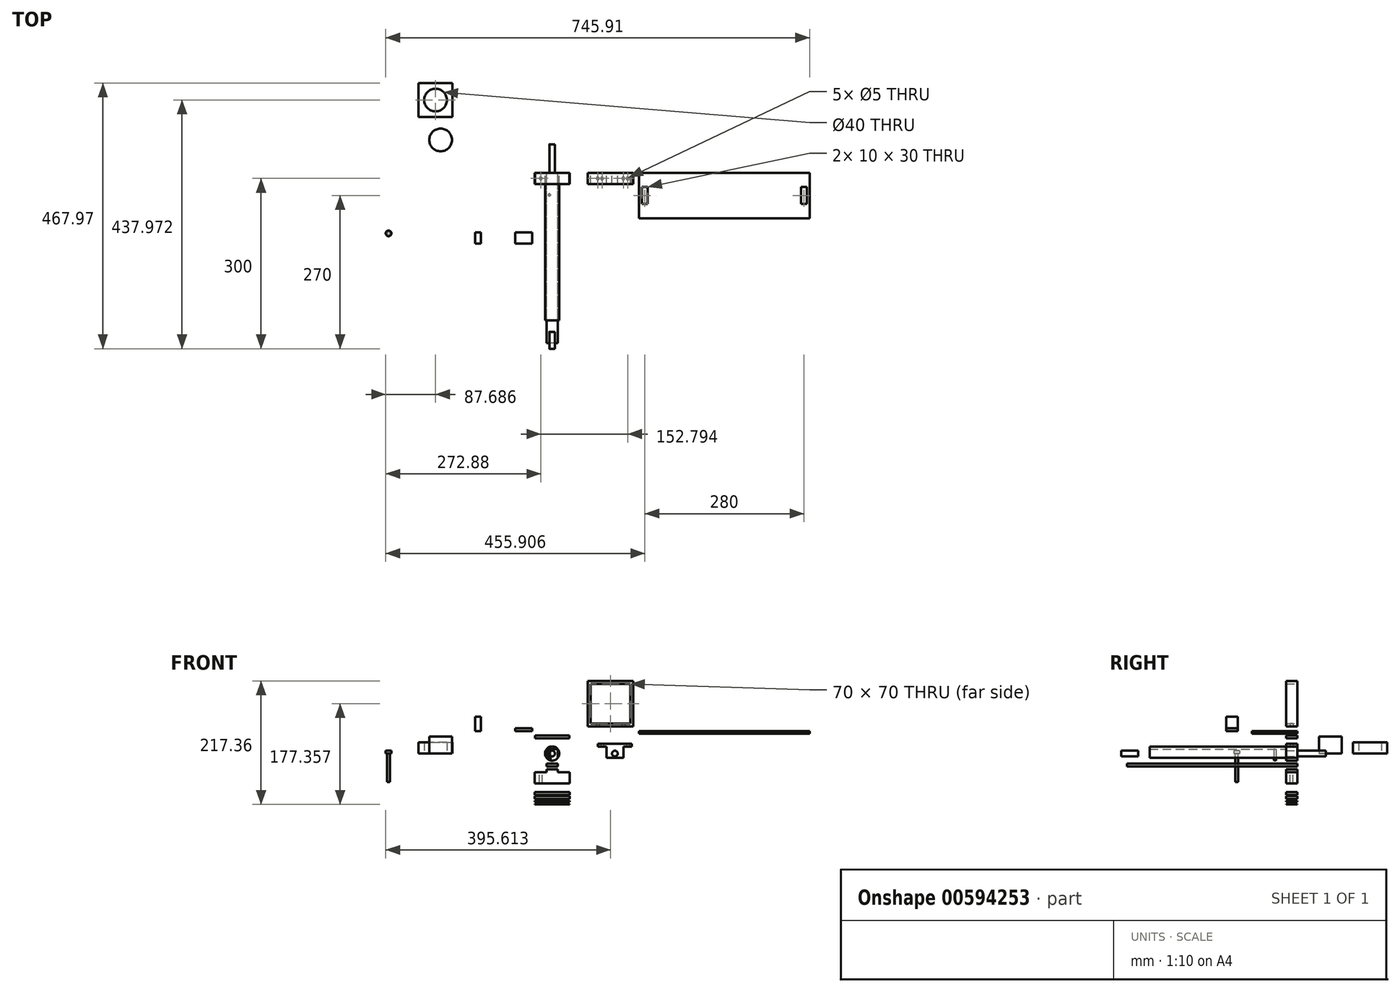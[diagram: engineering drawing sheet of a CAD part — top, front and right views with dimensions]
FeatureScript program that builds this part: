
annotation { "Feature Type Name" : "Feature", "Feature Type Description" : "" }
export const myFeature = defineFeature(function(context is Context, id is Id, definition is map)
    precondition{}
    {
        {
            var Q0;
            Q0=qCreatedBy(makeId("Front.planeOp"),FACE);
            var sketch = newSketch(context, id + "F0", { "sketchPlane" : qUnion([Q0])});
            skCircle(sketch, "E0", {"center": v(0, 0) * mm, "radius": 12.5 * mm});
            skCircle(sketch, "E1", {"center": v(110.3, 0) * mm, "radius": 5 * mm});
            skLineSegment(sketch, "E2.bottom", {"start": v(-30, 31.74) * mm, "end": v(30, 31.74) * mm});
            skLineSegment(sketch, "E2.top", {"start": v(-30, 26.74) * mm, "end": v(30, 26.74) * mm});
            skLineSegment(sketch, "E2.left", {"start": v(-30, 31.74) * mm, "end": v(-30, 26.74) * mm});
            skLineSegment(sketch, "E2.right", {"start": v(30, 31.74) * mm, "end": v(30, 26.74) * mm});
            skPoint(sketch, "E2.middle", {"position": v(0, 29.24) * mm});
            skLineSegment(sketch, "E3", {"start": v(110.3, 10) * mm, "end": v(110.3, -10) * mm, "construction": true});
            skCircle(sketch, "E4", {"center": v(110.3, 0) * mm, "radius": 12.5 * mm, "construction": true});
            skLineSegment(sketch, "E5", {"start": v(97.8, 0) * mm, "end": v(122.8, 0) * mm, "construction": true});
            skLineSegment(sketch, "E6", {"start": v(110.3, 12.5) * mm, "end": v(79.29, 12.5) * mm, "construction": true});
            skLineSegment(sketch, "E7", {"start": v(110.3, 5) * mm, "end": v(79.29, 5) * mm, "construction": true});
            skLineSegment(sketch, "E8", {"start": v(110.3, -5) * mm, "end": v(79.29, -5) * mm, "construction": true});
            skLineSegment(sketch, "E9", {"start": v(110.3, -12.5) * mm, "end": v(79.29, -12.5) * mm, "construction": true});
            skLineSegment(sketch, "E10", {"start": v(110.3, -7.5) * mm, "end": v(125.3, -7.5) * mm});
            skLineSegment(sketch, "E11", {"start": v(110.3, 17.5) * mm, "end": v(140.3, 17.5) * mm});
            skLineSegment(sketch, "E12", {"start": v(125.3, 12.5) * mm, "end": v(140.3, 12.5) * mm});
            skLineSegment(sketch, "E13", {"start": v(125.3, -7.5) * mm, "end": v(125.3, 12.5) * mm});
            skLineSegment(sketch, "E14", {"start": v(140.3, 17.5) * mm, "end": v(140.3, 12.5) * mm});
            skPoint(sketch, "E15.orphan", {"position": v(110.3, 12.5) * mm});
            skLineSegment(sketch, "E16.MirrorCS", {"start": v(95.3, 12.5) * mm, "end": v(80.3, 12.5) * mm});
            skLineSegment(sketch, "E17.MirrorCS", {"start": v(80.3, 17.5) * mm, "end": v(80.3, 12.5) * mm});
            skLineSegment(sketch, "E18.MirrorCS", {"start": v(110.3, 17.5) * mm, "end": v(80.3, 17.5) * mm});
            skLineSegment(sketch, "E19.MirrorCS", {"start": v(95.3, -7.5) * mm, "end": v(95.3, 12.5) * mm});
            skLineSegment(sketch, "E20.MirrorCS", {"start": v(110.3, -7.5) * mm, "end": v(95.3, -7.5) * mm});
            skLineSegment(sketch, "E21.top", {"start": v(0, -27.58) * mm, "end": v(10, -27.58) * mm});
            skLineSegment(sketch, "E22", {"start": v(10.93, -32.58) * mm, "end": v(30.93, -32.58) * mm});
            skLineSegment(sketch, "E23", {"start": v(30.93, -32.58) * mm, "end": v(30.93, -52.58) * mm});
            skLineSegment(sketch, "E24", {"start": v(30.93, -52.58) * mm, "end": v(0, -52.58) * mm});
            skLineSegment(sketch, "E25.MirrorCS", {"start": v(0, -27.58) * mm, "end": v(-10, -27.58) * mm});
            skLineSegment(sketch, "E26.MirrorCS", {"start": v(-10.93, -32.58) * mm, "end": v(-30.93, -32.58) * mm});
            skLineSegment(sketch, "E27.MirrorCS", {"start": v(-30.93, -32.58) * mm, "end": v(-30.93, -52.58) * mm});
            skLineSegment(sketch, "E28.MirrorCS", {"start": v(-30.93, -52.58) * mm, "end": v(0, -52.58) * mm});
            skLineSegment(sketch, "E29", {"start": v(0, -22.52) * mm, "end": v(10, -22.52) * mm});
            skLineSegment(sketch, "E30", {"start": v(10, -22.52) * mm, "end": v(10, -17.52) * mm});
            skLineSegment(sketch, "E31", {"start": v(10, -17.52) * mm, "end": v(0, -17.52) * mm});
            skLineSegment(sketch, "E32.MirrorCS", {"start": v(-10, -17.52) * mm, "end": v(0, -17.52) * mm});
            skLineSegment(sketch, "E33.MirrorCS", {"start": v(0, -22.52) * mm, "end": v(-10, -22.52) * mm});
            skLineSegment(sketch, "E34.MirrorCS", {"start": v(-10, -22.52) * mm, "end": v(-10, -17.52) * mm});
            skLineSegment(sketch, "E35.bottom", {"start": v(137.73, 52.7) * mm, "end": v(67.73, 52.7) * mm});
            skLineSegment(sketch, "E35.top", {"start": v(137.73, 122.7) * mm, "end": v(67.73, 122.7) * mm});
            skLineSegment(sketch, "E35.left", {"start": v(137.73, 52.7) * mm, "end": v(137.73, 122.7) * mm});
            skLineSegment(sketch, "E35.right", {"start": v(67.73, 52.7) * mm, "end": v(67.73, 122.7) * mm});
            skPoint(sketch, "E35.middle", {"position": v(102.73, 87.7) * mm});
            skLineSegment(sketch, "E36.bottom", {"start": v(62.73, 127.7) * mm, "end": v(142.73, 127.7) * mm});
            skLineSegment(sketch, "E36.top", {"start": v(62.73, 47.7) * mm, "end": v(142.73, 47.7) * mm});
            skLineSegment(sketch, "E36.left", {"start": v(62.73, 127.7) * mm, "end": v(62.73, 47.7) * mm});
            skLineSegment(sketch, "E36.right", {"start": v(142.73, 127.7) * mm, "end": v(142.73, 47.7) * mm});
            skLineSegment(sketch, "E37.bottom", {"start": v(-30.93, -79.86) * mm, "end": v(30.93, -79.86) * mm});
            skLineSegment(sketch, "E37.top", {"start": v(-30.93, -74.86) * mm, "end": v(30.93, -74.86) * mm});
            skLineSegment(sketch, "E37.left", {"start": v(-30.93, -79.86) * mm, "end": v(-30.93, -74.86) * mm});
            skLineSegment(sketch, "E37.right", {"start": v(30.93, -79.86) * mm, "end": v(30.93, -74.86) * mm});
            skLineSegment(sketch, "E38.MirrorCS", {"start": v(-30.74, -88.65) * mm, "end": v(31.12, -88.65) * mm});
            skLineSegment(sketch, "E39.MirrorCS", {"start": v(-30.74, -89.65) * mm, "end": v(31.12, -89.65) * mm});
            skLineSegment(sketch, "E40", {"start": v(-30.93, -82.76) * mm, "end": v(30.93, -82.76) * mm});
            skLineSegment(sketch, "E41", {"start": v(30.93, -82.76) * mm, "end": v(30.93, -84.76) * mm});
            skLineSegment(sketch, "E42", {"start": v(30.93, -84.76) * mm, "end": v(-30.93, -84.76) * mm});
            skLineSegment(sketch, "E43", {"start": v(-30.93, -84.76) * mm, "end": v(-30.93, -82.76) * mm});
            skLineSegment(sketch, "E44", {"start": v(-30.74, -88.65) * mm, "end": v(-30.74, -89.65) * mm});
            skLineSegment(sketch, "E45", {"start": v(31.12, -88.65) * mm, "end": v(31.12, -89.65) * mm});
            skLineSegment(sketch, "E46", {"start": v(-30.93, -72.74) * mm, "end": v(30.93, -72.74) * mm});
            skLineSegment(sketch, "E47", {"start": v(30.93, -72.74) * mm, "end": v(30.93, -67.74) * mm});
            skLineSegment(sketch, "E48", {"start": v(30.93, -67.74) * mm, "end": v(-30.93, -67.74) * mm});
            skLineSegment(sketch, "E49", {"start": v(-30.93, -67.74) * mm, "end": v(-30.93, -72.74) * mm});
            skLineSegment(sketch, "E50", {"start": v(-10, -27.58) * mm, "end": v(-10, -32.58) * mm});
            skLineSegment(sketch, "E51", {"start": v(-10, -32.58) * mm, "end": v(-10.93, -32.58) * mm});
            skPoint(sketch, "E52.MirrorCS.end.orphan", {"position": v(-10, -27.58) * mm});
            skPoint(sketch, "E52.MirrorCS.start.orphan", {"position": v(-10.93, -32.58) * mm});
            skLineSegment(sketch, "E53", {"start": v(10, -27.58) * mm, "end": v(10, -32.58) * mm});
            skLineSegment(sketch, "E54", {"start": v(10, -32.58) * mm, "end": v(10.93, -32.58) * mm});
            skLineSegment(sketch, "E55.left", {"start": v(194.47, 95.4) * mm, "end": v(194.47, 97.9) * mm});
            skLineSegment(sketch, "E56.bottom", {"start": v(-122.7, 157) * mm, "end": v(-422.7, 157) * mm});
            skLineSegment(sketch, "E56.top", {"start": v(-122.7, 159.5) * mm, "end": v(-422.7, 159.5) * mm});
            skLineSegment(sketch, "E56.left", {"start": v(-122.7, 157) * mm, "end": v(-122.7, 159.5) * mm});
            skLineSegment(sketch, "E56.right", {"start": v(-422.7, 157) * mm, "end": v(-422.7, 159.5) * mm});
            skLineSegment(sketch, "E57", {"start": v(-272.7, 150) * mm, "end": v(-272.7, 153.49) * mm, "construction": true});
            skPoint(sketch, "E57.startSnap0", {"position": v(-272.7, 157) * mm});
            skSolve(sketch);
        }
        {
            var Q0;
            Q0=makeQuery(id+"F0.imprint","IMPRINT",FACE,{"disambiguationData":[TD([[makeQuery(id+"F0.imprint","IMPRINT",EDGE,{"derivedFrom":sQuery(id+"F0.wireOp",EDGE,"E1")}),-1.0]])]});
            var Q1;
            Q1=makeQuery(id+"F0.imprint","IMPRINT",FACE,{"disambiguationData":[TD([[makeQuery(id+"F0.imprint","IMPRINT",EDGE,{"derivedFrom":sQuery(id+"F0.wireOp",EDGE,"E2.bottom")}),-1.0]])]});
            var Q2;
            Q2=makeQuery(id+"F0.imprint","IMPRINT",FACE,{"disambiguationData":[TD([[makeQuery(id+"F0.imprint","IMPRINT",EDGE,{"derivedFrom":sQuery(id+"F0.wireOp",EDGE,"E21.top")}),-1.0]])]});
            var Q3;
            Q3=makeQuery(id+"F0.imprint","IMPRINT",FACE,{"disambiguationData":[TD([[makeQuery(id+"F0.imprint","IMPRINT",EDGE,{"derivedFrom":sQuery(id+"F0.wireOp",EDGE,"E35.bottom")}),1.0]])]});
            var Q4;
            Q4=makeQuery(id+"F0.imprint","IMPRINT",FACE,{"disambiguationData":[TD([[makeQuery(id+"F0.imprint","IMPRINT",EDGE,{"derivedFrom":sQuery(id+"F0.wireOp",EDGE,"E37.bottom")}),1.0]])]});
            var Q5;
            Q5=makeQuery(id+"F0.imprint","IMPRINT",FACE,{"disambiguationData":[TD([[makeQuery(id+"F0.imprint","IMPRINT",EDGE,{"derivedFrom":sQuery(id+"F0.wireOp",EDGE,"E38.MirrorCS")}),-1.0]])]});
            var Q6;
            Q6=makeQuery(id+"F0.imprint","IMPRINT",FACE,{"disambiguationData":[TD([[makeQuery(id+"F0.imprint","IMPRINT",EDGE,{"derivedFrom":sQuery(id+"F0.wireOp",EDGE,"E40")}),-1.0]])]});
            var Q7;
            Q7=makeQuery(id+"F0.imprint","IMPRINT",FACE,{"disambiguationData":[TD([[makeQuery(id+"F0.imprint","IMPRINT",EDGE,{"derivedFrom":sQuery(id+"F0.wireOp",EDGE,"E46")}),1.0]])]});
            var Q8;
            {var subQ5=sQuery(id+"F0.wireOp",EDGE,"E55.right");Q8=makeQuery(id+"F0.imprint","IMPRINT",FACE,{"disambiguationData":[TD([[makeQuery(id+"F0.imprint","IMPRINT",EDGE,{"derivedFrom":subQ5}),-1.0]])]});}
            extrude(context, id + "F1", {"entities" : qUnion([Q0, Q1, Q2, Q3, Q4, Q5, Q6, Q7, Q8]), "depth" : 20 * mm, "offsetDistance" : 25 * mm});
        }
        {
            var Q0;
            Q0=makeQuery(id+"F0.imprint","IMPRINT",FACE,{"disambiguationData":[TD([[makeQuery(id+"F0.imprint","IMPRINT",EDGE,{"derivedFrom":sQuery(id+"F0.wireOp",EDGE,"E0")}),1.0]])]});
            extrude(context, id + "F2", {"entities" : qUnion([Q0]), "depth" : 260 * mm, "offsetDistance" : 25 * mm});
        }
        {
            var Q0;
            Q0=makeQuery(id+"F2.opExtrude","CAP_FACE",FACE,{"disambiguationData":[OSD([sQuery(id+"F0.wireOp",EDGE,"E0")])],"isStart":false});
            var sketch = newSketch(context, id + "F3", { "sketchPlane" : qUnion([Q0])});
            skCircle(sketch, "E58", {"center": v(0, 0) * mm, "radius": 5 * mm});
            skSolve(sketch);
        }
        {
            var Q0;
            Q0=makeQuery(id+"F3.imprint","IMPRINT",FACE,{"disambiguationData":[TD([[makeQuery(id+"F3.imprint","IMPRINT",EDGE,{"derivedFrom":sQuery(id+"F3.wireOp",EDGE,"E58")}),1.0]])]});
            extrude(context, id + "F4", {"entities" : qUnion([Q0]), "operationType" : NewBodyOperationType.ADD, "depth" : 50 * mm, "offsetDistance" : 25 * mm});
        }
        {
            var Q0;
            Q0=makeQuery(id+"F0.imprint","IMPRINT",FACE,{"disambiguationData":[TD([[makeQuery(id+"F0.imprint","IMPRINT",EDGE,{"derivedFrom":sQuery(id+"F0.wireOp",EDGE,"E29")}),1.0]])]});
            extrude(context, id + "F5", {"entities" : qUnion([Q0]), "depth" : 300 * mm, "offsetDistance" : 25 * mm});
        }
        {
            var Q0;
            Q0=makeQuery(id+"F1.opExtrude","SWEPT_FACE",FACE,{"disambiguationData":[OSD([sQuery(id+"F0.wireOp",EDGE,"E26.MirrorCS")])]});
            var sketch = newSketch(context, id + "F6", { "sketchPlane" : qUnion([Q0])});
            skCircle(sketch, "E59", {"center": v(-20, -10) * mm, "radius": 2.5 * mm});
            skSolve(sketch);
        }
        {
            var Q0;
            Q0=makeQuery(id+"F6.imprint","IMPRINT",FACE,{"disambiguationData":[TD([[makeQuery(id+"F6.imprint","IMPRINT",EDGE,{"derivedFrom":sQuery(id+"F6.wireOp",EDGE,"E59")}),1.0]])]});
            var Q1;
            Q1=makeQuery(id+"FNYWGUJzlf6PVvf_4.imprint","IMPRINT",FACE,{"disambiguationData":[TD([[makeQuery(id+"FNYWGUJzlf6PVvf_4.imprint","IMPRINT",EDGE,{"derivedFrom":sQuery(id+"FNYWGUJzlf6PVvf_4.wireOp",EDGE,"JrdPBHnR-5tIZ-cZ5f-IPz8-CMVoVNEgzM20")}),1.0]])]});
            extrude(context, id + "F7", {"entities" : qUnion([Q0, Q1]), "operationType" : NewBodyOperationType.REMOVE, "oppositeDirection" : true, "depth" : 25 * mm, "offsetDistance" : 25 * mm});
        }
        {
            var Q0;
            Q0=makeQuery(id+"F1.opExtrude","SWEPT_FACE",FACE,{"disambiguationData":[OSD([sQuery(id+"F0.wireOp",EDGE,"E12")])]});
            var sketch = newSketch(context, id + "F8", { "sketchPlane" : qUnion([Q0])});
            skCircle(sketch, "E60", {"center": v(132.8, 10) * mm, "radius": 2.5 * mm});
            skPoint(sketch, "E60.centerSnap0", {"position": v(132.8, 20) * mm});
            skPoint(sketch, "E60.centerSnap1", {"position": v(125.3, 10) * mm});
            skSolve(sketch);
        }
        {
            var Q0;
            Q0=makeQuery(id+"F1.opExtrude","SWEPT_FACE",FACE,{"disambiguationData":[OSD([sQuery(id+"F0.wireOp",EDGE,"E16.MirrorCS")])]});
            var sketch = newSketch(context, id + "F9", { "sketchPlane" : qUnion([Q0])});
            skCircle(sketch, "E61", {"center": v(87.8, 10) * mm, "radius": 2.5 * mm});
            skPoint(sketch, "E61.centerSnap0", {"position": v(80.3, 10) * mm});
            skPoint(sketch, "E61.centerSnap1", {"position": v(87.8, 20) * mm});
            skSolve(sketch);
        }
        {
            var Q0;
            Q0=makeQuery(id+"F9.imprint","IMPRINT",FACE,{"disambiguationData":[TD([[makeQuery(id+"F9.imprint","IMPRINT",EDGE,{"derivedFrom":sQuery(id+"F9.wireOp",EDGE,"E61")}),1.0]])]});
            var Q1;
            Q1=makeQuery(id+"F8.imprint","IMPRINT",FACE,{"disambiguationData":[TD([[makeQuery(id+"F8.imprint","IMPRINT",EDGE,{"derivedFrom":sQuery(id+"F8.wireOp",EDGE,"E60")}),1.0]])]});
            extrude(context, id + "F10", {"entities" : qUnion([Q0, Q1]), "operationType" : NewBodyOperationType.REMOVE, "oppositeDirection" : true, "depth" : 25 * mm, "offsetDistance" : 25 * mm});
        }
        {
            var Q0;
            Q0=makeQuery(id+"F5.opExtrude","SWEPT_FACE",FACE,{"disambiguationData":[OSD([sQuery(id+"F0.wireOp",EDGE,"E31"),sQuery(id+"F0.wireOp",EDGE,"E32.MirrorCS")])]});
            var sketch = newSketch(context, id + "F11", { "sketchPlane" : qUnion([Q0])});
            skLineSegment(sketch, "E62", {"start": v(-10, -280) * mm, "end": v(10, -280) * mm});
            skCircle(sketch, "E63", {"center": v(5, -39.13) * mm, "radius": 1.93 * mm});
            skPoint(sketch, "E64.orphan", {"position": v(0, -300) * mm});
            skCircle(sketch, "E65.MirrorC", {"center": v(-5, -39.13) * mm, "radius": 1.93 * mm});
            skLineSegment(sketch, "E66", {"start": v(10, -20) * mm, "end": v(-10, -20) * mm});
            skSolve(sketch);
        }
        {
            var Q0;
            Q0=makeQuery(id+"F11.imprint","IMPRINT",FACE,{"disambiguationData":[TD([[makeQuery(id+"F11.imprint","IMPRINT",EDGE,{"derivedFrom":sQuery(id+"F11.wireOp",EDGE,"E65.MirrorC")}),-1.0]])]});
            var Q1;
            Q1=makeQuery(id+"F11.imprint","IMPRINT",FACE,{"disambiguationData":[TD([[makeQuery(id+"F11.imprint","IMPRINT",EDGE,{"derivedFrom":sQuery(id+"F11.wireOp",EDGE,"E63")}),1.0]])]});
            extrude(context, id + "F12", {"entities" : qUnion([Q0, Q1]), "operationType" : NewBodyOperationType.REMOVE, "depth" : 25 * mm, "offsetDistance" : 25 * mm});
        }
        {
            var Q0;
            Q0=makeQuery(id+"F1.opExtrude","SWEPT_FACE",FACE,{"disambiguationData":[OSD([sQuery(id+"F0.wireOp",EDGE,"E36.top")])]});
            var sketch = newSketch(context, id + "F13", { "sketchPlane" : qUnion([Q0])});
            skCircle(sketch, "E67", {"center": v(80.23, 10) * mm, "radius": 2.5 * mm});
            skCircle(sketch, "E68", {"center": v(125.23, 10) * mm, "radius": 2.5 * mm});
            skLineSegment(sketch, "E69", {"start": v(62.73, 20) * mm, "end": v(142.73, 20) * mm, "construction": true});
            skLineSegment(sketch, "E70", {"start": v(142.73, 20) * mm, "end": v(142.73, 0) * mm, "construction": true});
            skLineSegment(sketch, "E71", {"start": v(142.73, 0) * mm, "end": v(62.73, 0) * mm, "construction": true});
            skLineSegment(sketch, "E72", {"start": v(62.73, 0) * mm, "end": v(62.73, 20) * mm, "construction": true});
            skLineSegment(sketch, "E73", {"start": v(67.73, 20) * mm, "end": v(67.73, 0) * mm, "construction": true});
            skLineSegment(sketch, "E74", {"start": v(137.73, 20) * mm, "end": v(137.73, 0) * mm, "construction": true});
            skSolve(sketch);
        }
        {
            var Q0;
            Q0=makeQuery(id+"F2.opExtrude","CAP_FACE",FACE,{"disambiguationData":[OSD([sQuery(id+"F0.wireOp",EDGE,"E0")])],"isStart":true});
            var sketch = newSketch(context, id + "F14", { "sketchPlane" : qUnion([Q0])});
            skCircle(sketch, "E75", {"center": v(0, 0) * mm, "radius": 5 * mm});
            skSolve(sketch);
        }
        {
            var Q0;
            Q0=qSketchRegion(id+"F14",true);
            extrude(context, id + "F15", {"entities" : qUnion([Q0]), "operationType" : NewBodyOperationType.ADD, "depth" : 50 * mm, "offsetDistance" : 25 * mm});
        }
        {
            var Q0;
            Q0=qCreatedBy(makeId("Front.planeOp"),FACE);
            var sketch = newSketch(context, id + "F16", { "sketchPlane" : qUnion([Q0])});
            skLineSegment(sketch, "E76.bottom", {"start": v(153.03, 39.78) * mm, "end": v(453.03, 39.78) * mm});
            skLineSegment(sketch, "E76.top", {"start": v(153.03, 34.78) * mm, "end": v(453.03, 34.78) * mm});
            skLineSegment(sketch, "E76.left", {"start": v(153.03, 39.78) * mm, "end": v(153.03, 34.78) * mm});
            skLineSegment(sketch, "E76.right", {"start": v(453.03, 39.78) * mm, "end": v(453.03, 34.78) * mm});
            skSolve(sketch);
        }
        {
            var Q0;
            Q0=makeQuery(id+"F16.imprint","IMPRINT",FACE,{"disambiguationData":[TD([[makeQuery(id+"F16.imprint","IMPRINT",EDGE,{"derivedFrom":sQuery(id+"F16.wireOp",EDGE,"E76.bottom")}),-1.0]])]});
            extrude(context, id + "F17", {"entities" : qUnion([Q0]), "depth" : 80 * mm, "offsetDistance" : 25 * mm});
        }
        {
            var Q0;
            Q0=makeQuery(id+"F17.opExtrude","SWEPT_FACE",FACE,{"disambiguationData":[OSD([sQuery(id+"F16.wireOp",EDGE,"E76.bottom")])]});
            var sketch = newSketch(context, id + "F18", { "sketchPlane" : qUnion([Q0])});
            skLineSegment(sketch, "E77", {"start": v(173.03, 0) * mm, "end": v(173.03, -80) * mm});
            skLineSegment(sketch, "E78.bottom", {"start": v(158.03, -25) * mm, "end": v(168.03, -25) * mm});
            skLineSegment(sketch, "E78.top", {"start": v(158.03, -55) * mm, "end": v(168.03, -55) * mm});
            skLineSegment(sketch, "E78.left", {"start": v(158.03, -25) * mm, "end": v(158.03, -55) * mm});
            skLineSegment(sketch, "E78.right", {"start": v(168.03, -25) * mm, "end": v(168.03, -55) * mm});
            skPoint(sketch, "E78.middle", {"position": v(163.03, -40) * mm});
            skLineSegment(sketch, "E79", {"start": v(303.03, 0) * mm, "end": v(303.03, -80) * mm, "construction": true});
            skLineSegment(sketch, "E80.MirrorCS", {"start": v(438.03, -25) * mm, "end": v(438.03, -55) * mm});
            skLineSegment(sketch, "E81.MirrorCS", {"start": v(448.03, -25) * mm, "end": v(438.03, -25) * mm});
            skLineSegment(sketch, "E82.MirrorCS", {"start": v(448.03, -25) * mm, "end": v(448.03, -55) * mm});
            skLineSegment(sketch, "E83.MirrorCS", {"start": v(448.03, -55) * mm, "end": v(438.03, -55) * mm});
            skLineSegment(sketch, "E84.MirrorCS", {"start": v(433.03, 0) * mm, "end": v(433.03, -80) * mm});
            skLineSegment(sketch, "E85.bottom", {"start": v(-65.07, -104.85) * mm, "end": v(-35.07, -104.85) * mm});
            skLineSegment(sketch, "E85.top", {"start": v(-65.07, -124.85) * mm, "end": v(-35.07, -124.85) * mm});
            skLineSegment(sketch, "E85.left", {"start": v(-65.07, -104.85) * mm, "end": v(-65.07, -124.85) * mm});
            skLineSegment(sketch, "E85.right", {"start": v(-35.07, -104.85) * mm, "end": v(-35.07, -124.85) * mm});
            skLineSegment(sketch, "E86.bottom", {"start": v(-135.53, -104.85) * mm, "end": v(-125.53, -104.85) * mm});
            skLineSegment(sketch, "E86.top", {"start": v(-135.53, -124.85) * mm, "end": v(-125.53, -124.85) * mm});
            skLineSegment(sketch, "E86.left", {"start": v(-135.53, -104.85) * mm, "end": v(-135.53, -124.85) * mm});
            skLineSegment(sketch, "E86.right", {"start": v(-125.53, -104.85) * mm, "end": v(-125.53, -124.85) * mm});
            skSolve(sketch);
        }
        {
            var Q0;
            Q0=qCreatedBy(makeId("Top.planeOp"),FACE);
            var sketch = newSketch(context, id + "F19", { "sketchPlane" : qUnion([Q0])});
            skCircle(sketch, "E87", {"center": v(-196.25, 57.8) * mm, "radius": 20 * mm});
            skLineSegment(sketch, "E88.bottom", {"start": v(-235.2, 97.97) * mm, "end": v(-175.2, 97.97) * mm});
            skLineSegment(sketch, "E88.top", {"start": v(-235.2, 157.97) * mm, "end": v(-175.2, 157.97) * mm});
            skLineSegment(sketch, "E88.left", {"start": v(-235.2, 97.97) * mm, "end": v(-235.2, 157.97) * mm});
            skLineSegment(sketch, "E88.right", {"start": v(-175.2, 97.97) * mm, "end": v(-175.2, 157.97) * mm});
            skCircle(sketch, "E89", {"center": v(-205.2, 127.97) * mm, "radius": 20 * mm});
            skPoint(sketch, "E89.centerSnap0", {"position": v(-175.2, 127.97) * mm});
            skPoint(sketch, "E89.centerSnap1", {"position": v(-205.2, 97.97) * mm});
            skSolve(sketch);
        }
        {
            var Q0;
            Q0=makeQuery(id+"F19.imprint","IMPRINT",FACE,{"disambiguationData":[TD([[makeQuery(id+"F19.imprint","IMPRINT",EDGE,{"derivedFrom":sQuery(id+"F19.wireOp",EDGE,"E87")}),1.0]])]});
            extrude(context, id + "F20", {"entities" : qUnion([Q0]), "depth" : 30 * mm, "offsetDistance" : 25 * mm});
        }
        {
            var Q0;
            Q0=makeQuery(id+"F19.imprint","IMPRINT",FACE,{"disambiguationData":[TD([[makeQuery(id+"F19.imprint","IMPRINT",EDGE,{"derivedFrom":sQuery(id+"F19.wireOp",EDGE,"E88.bottom")}),1.0]])]});
            extrude(context, id + "F21", {"entities" : qUnion([Q0]), "depth" : 20 * mm, "offsetDistance" : 25 * mm});
        }
        {
            var Q0;
            Q0=makeQuery(id+"F18.imprint","IMPRINT",FACE,{"disambiguationData":[TD([[makeQuery(id+"F18.imprint","IMPRINT",EDGE,{"derivedFrom":sQuery(id+"F18.wireOp",EDGE,"E78.bottom")}),-1.0]])]});
            var Q1;
            Q1=makeQuery(id+"F18.imprint","IMPRINT",FACE,{"disambiguationData":[TD([[makeQuery(id+"F18.imprint","IMPRINT",EDGE,{"derivedFrom":sQuery(id+"F18.wireOp",EDGE,"E80.MirrorCS")}),1.0]])]});
            extrude(context, id + "F22", {"entities" : qUnion([Q0, Q1]), "operationType" : NewBodyOperationType.REMOVE, "endBound" : BoundingType.THROUGH_ALL, "oppositeDirection" : true, "depth" : 25 * mm, "offsetDistance" : 25 * mm});
        }
        {
            var Q0;
            Q0=makeQuery(id+"F18.imprint","IMPRINT",FACE,{"disambiguationData":[TD([[makeQuery(id+"F18.imprint","IMPRINT",EDGE,{"derivedFrom":sQuery(id+"F18.wireOp",EDGE,"E86.bottom")}),-1.0]])]});
            extrude(context, id + "F23", {"entities" : qUnion([Q0]), "depth" : 25 * mm, "offsetDistance" : 25 * mm});
        }
        {
            var Q0;
            Q0=makeQuery(id+"F18.imprint","IMPRINT",FACE,{"disambiguationData":[TD([[makeQuery(id+"F18.imprint","IMPRINT",EDGE,{"derivedFrom":sQuery(id+"F18.wireOp",EDGE,"E85.bottom")}),-1.0]])]});
            extrude(context, id + "F24", {"entities" : qUnion([Q0]), "depth" : 5 * mm, "offsetDistance" : 25 * mm});
        }
        {
            var Q0;
            Q0=makeQuery(id+"F13.imprint","IMPRINT",FACE,{"disambiguationData":[TD([[makeQuery(id+"F13.imprint","IMPRINT",EDGE,{"derivedFrom":sQuery(id+"F13.wireOp",EDGE,"E68")}),1.0]])]});
            var Q1;
            Q1=makeQuery(id+"F13.imprint","IMPRINT",FACE,{"disambiguationData":[TD([[makeQuery(id+"F13.imprint","IMPRINT",EDGE,{"derivedFrom":sQuery(id+"F13.wireOp",EDGE,"E67")}),1.0]])]});
            extrude(context, id + "F25", {"entities" : qUnion([Q0, Q1]), "operationType" : NewBodyOperationType.REMOVE, "endBound" : BoundingType.UP_TO_NEXT, "oppositeDirection" : true, "depth" : 25 * mm, "offsetDistance" : 25 * mm});
        }
        {
            var Q0;
            Q0=qCreatedBy(makeId("Top.planeOp"),FACE);
            var sketch = newSketch(context, id + "F26", { "sketchPlane" : qUnion([Q0])});
            skCircle(sketch, "E90", {"center": v(-287.88, -106.71) * mm, "radius": 5 * mm});
            skSolve(sketch);
        }
        {
            var Q0;
            Q0=makeQuery(id+"F26.imprint","IMPRINT",FACE,{"disambiguationData":[TD([[makeQuery(id+"F26.imprint","IMPRINT",EDGE,{"derivedFrom":sQuery(id+"F26.wireOp",EDGE,"E90")}),1.0]])]});
            extrude(context, id + "F27", {"entities" : qUnion([Q0]), "depth" : 5 * mm, "offsetDistance" : 25 * mm});
        }
        {
            var Q0;
            Q0=makeQuery(id+"F26.imprint","IMPRINT",FACE,{"disambiguationData":[TD([[makeQuery(id+"F26.imprint","IMPRINT",EDGE,{"derivedFrom":sQuery(id+"F26.wireOp",EDGE,"E90")}),1.0]])]});
            var sketch = newSketch(context, id + "F28", { "sketchPlane" : qUnion([Q0])});
            skCircle(sketch, "E91", {"center": v(-287.73, -106.85) * mm, "radius": 2.5 * mm});
            skSolve(sketch);
        }
        {
            var Q0;
            Q0=makeQuery(id+"F28.imprint","IMPRINT",FACE,{"disambiguationData":[TD([[makeQuery(id+"F28.imprint","IMPRINT",EDGE,{"derivedFrom":sQuery(id+"F28.wireOp",EDGE,"E91")}),1.0]])]});
            extrude(context, id + "F29", {"entities" : qUnion([Q0]), "operationType" : NewBodyOperationType.ADD, "oppositeDirection" : true, "depth" : 50 * mm, "offsetDistance" : 25 * mm});
        }
    });
